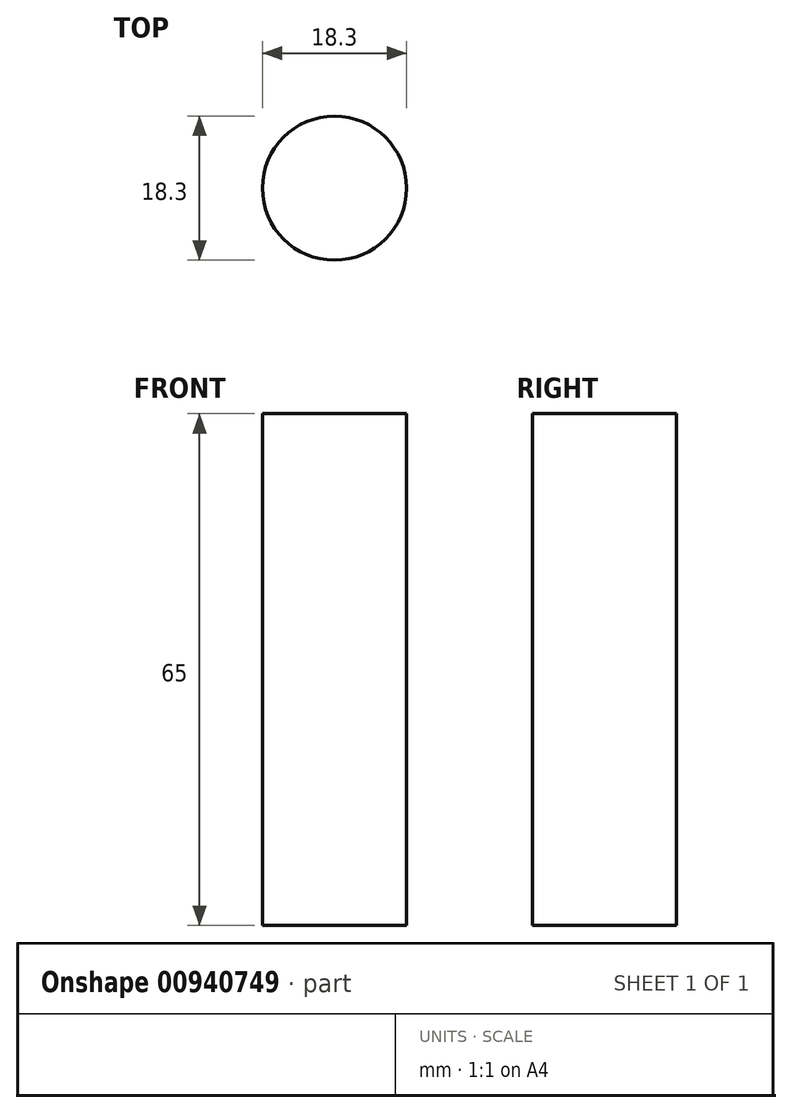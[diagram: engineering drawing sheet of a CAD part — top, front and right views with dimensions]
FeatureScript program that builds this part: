
annotation { "Feature Type Name" : "Feature", "Feature Type Description" : "" }
export const myFeature = defineFeature(function(context is Context, id is Id, definition is map)
    precondition{}
    {
        {
            var Q0;
            Q0=qCreatedBy(makeId("Top.planeOp"),FACE);
            var sketch = newSketch(context, id + "F0", { "sketchPlane" : qUnion([Q0])});
            skCircle(sketch, "E0", {"center": v(0, 0) * mm, "radius": 9.15 * mm});
            skSolve(sketch);
        }
        {
            var Q0;
            Q0=makeQuery(id+"F0.imprint","IMPRINT",FACE,{"disambiguationData":[TD([[makeQuery(id+"F0.imprint","IMPRINT",EDGE,{"derivedFrom":sQuery(id+"F0.wireOp",EDGE,"E0")}),1.0]])]});
            extrude(context, id + "F1", {"entities" : qUnion([Q0]), "depth" : 65 * mm, "offsetDistance" : 25 * mm});
        }
    });
